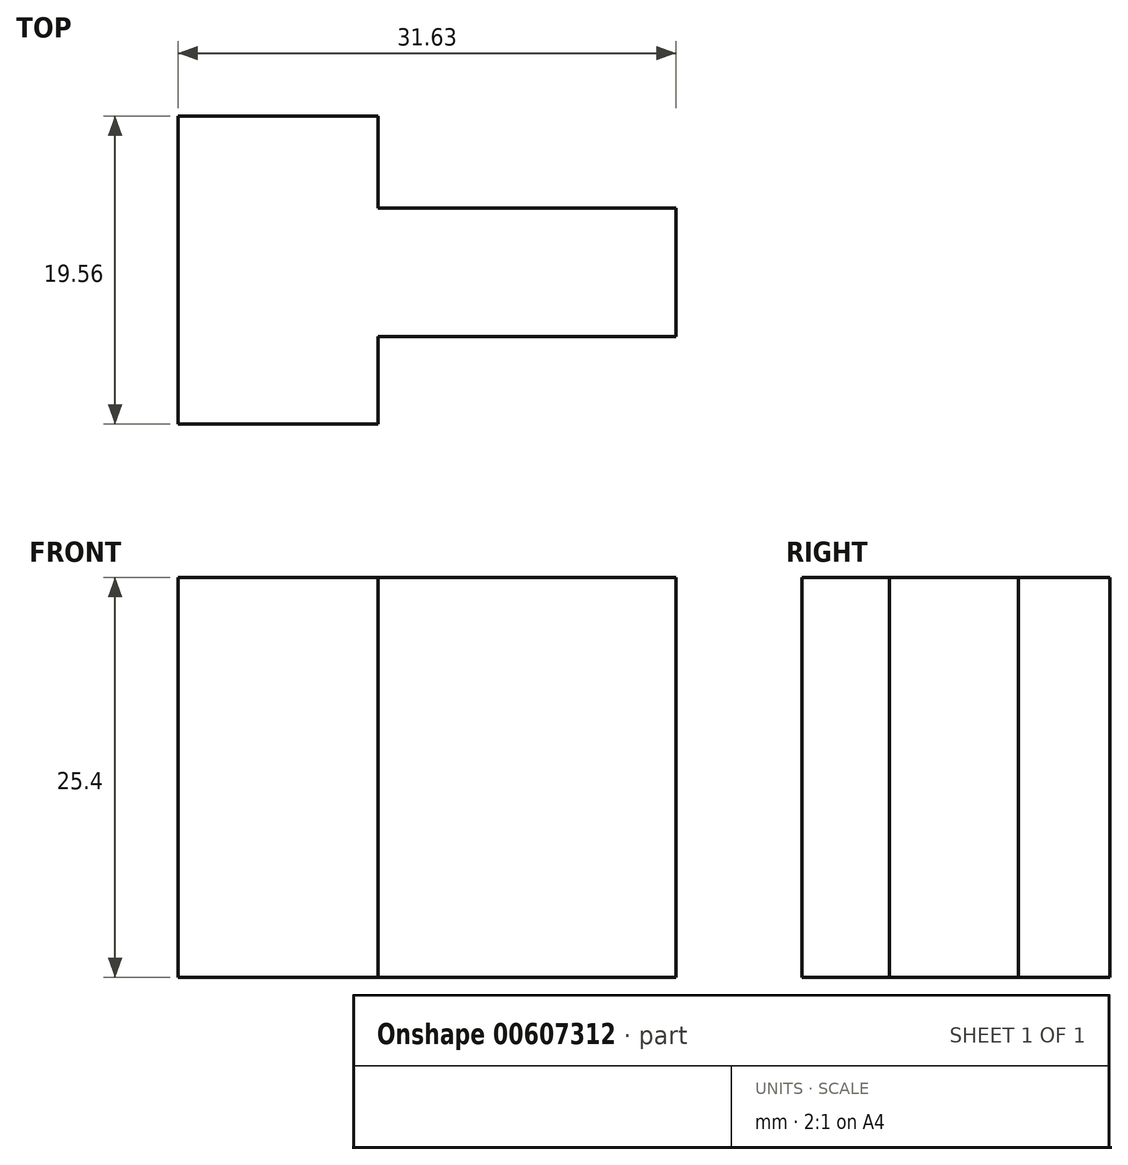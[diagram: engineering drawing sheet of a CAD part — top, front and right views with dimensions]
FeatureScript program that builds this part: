
annotation { "Feature Type Name" : "Feature", "Feature Type Description" : "" }
export const myFeature = defineFeature(function(context is Context, id is Id, definition is map)
    precondition{}
    {
        {
            var Q0;
            Q0=qCreatedBy(makeId("Top.planeOp"),FACE);
            var sketch = newSketch(context, id + "F0", { "sketchPlane" : qUnion([Q0])});
            skLineSegment(sketch, "E0", {"start": v(0, 0) * mm, "end": v(0, 19.56) * mm});
            skLineSegment(sketch, "E1", {"start": v(0, 19.56) * mm, "end": v(12.7, 19.56) * mm});
            skLineSegment(sketch, "E2", {"start": v(12.7, 19.56) * mm, "end": v(12.7, 13.72) * mm});
            skLineSegment(sketch, "E3", {"start": v(12.7, 13.72) * mm, "end": v(26.38, 13.72) * mm});
            skLineSegment(sketch, "E4", {"start": v(26.38, 13.72) * mm, "end": v(31.63, 13.72) * mm});
            skLineSegment(sketch, "E5", {"start": v(31.63, 13.72) * mm, "end": v(31.63, 5.55) * mm});
            skLineSegment(sketch, "E6", {"start": v(31.63, 5.55) * mm, "end": v(12.7, 5.55) * mm});
            skLineSegment(sketch, "E7", {"start": v(12.7, 5.55) * mm, "end": v(12.7, 0) * mm});
            skLineSegment(sketch, "E8", {"start": v(12.7, 0) * mm, "end": v(0, 0) * mm});
            skSolve(sketch);
        }
        {
            var Q0;
            Q0 = qSketchRegion(id + "F0", true);
            extrude(context, id + "F1", {"entities" : qUnion([Q0]), "depth" : 25.4 * mm, "offsetDistance" : 25.4 * mm});
        }
    });
